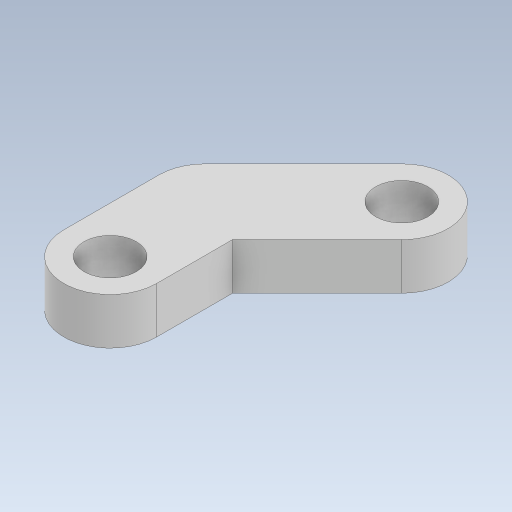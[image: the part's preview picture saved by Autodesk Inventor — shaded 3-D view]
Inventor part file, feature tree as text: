
AUTODESK INVENTOR PART (.ipt)
format: ipt  version: 2023 (Build 270158000, 158)  size: 111,104 bytes
history: native  units: in
note: dims shown in document units (in); Inventor stores cm internally (conversion verified against a paired STEP export)
features: sketch x2, extrude x1, hole x1
ambient origin geometry x8: Origin, YZ Plane, XZ Plane, XY Plane, X Axis, Y Axis, Z Axis, Center Point
bodies: Solid1 (feature_tree)
feature tree (4):
  extrude  "Extrusion1"  Depth=0.4724in
  hole  "Hole1"  [1 undecoded]
  sketch  "Sketch1"  dims[d0=0.4724in d1=0.5in]
  sketch  "Sketch2"  dims[d2=0.9843in d3=135.0deg d4=0.2362in d5=0.0in d6=0.2362in d7=0.266in d8=0.2362in d9=0.507in d10=0.0787in d11=0.5635in d12=0.5in d13=0.8108in]
note: 1 required parameter value undecoded (feature->parameter linkage not recoverable at this tier; creation-order binding heuristic only, values carry confidence <= 0.55)
